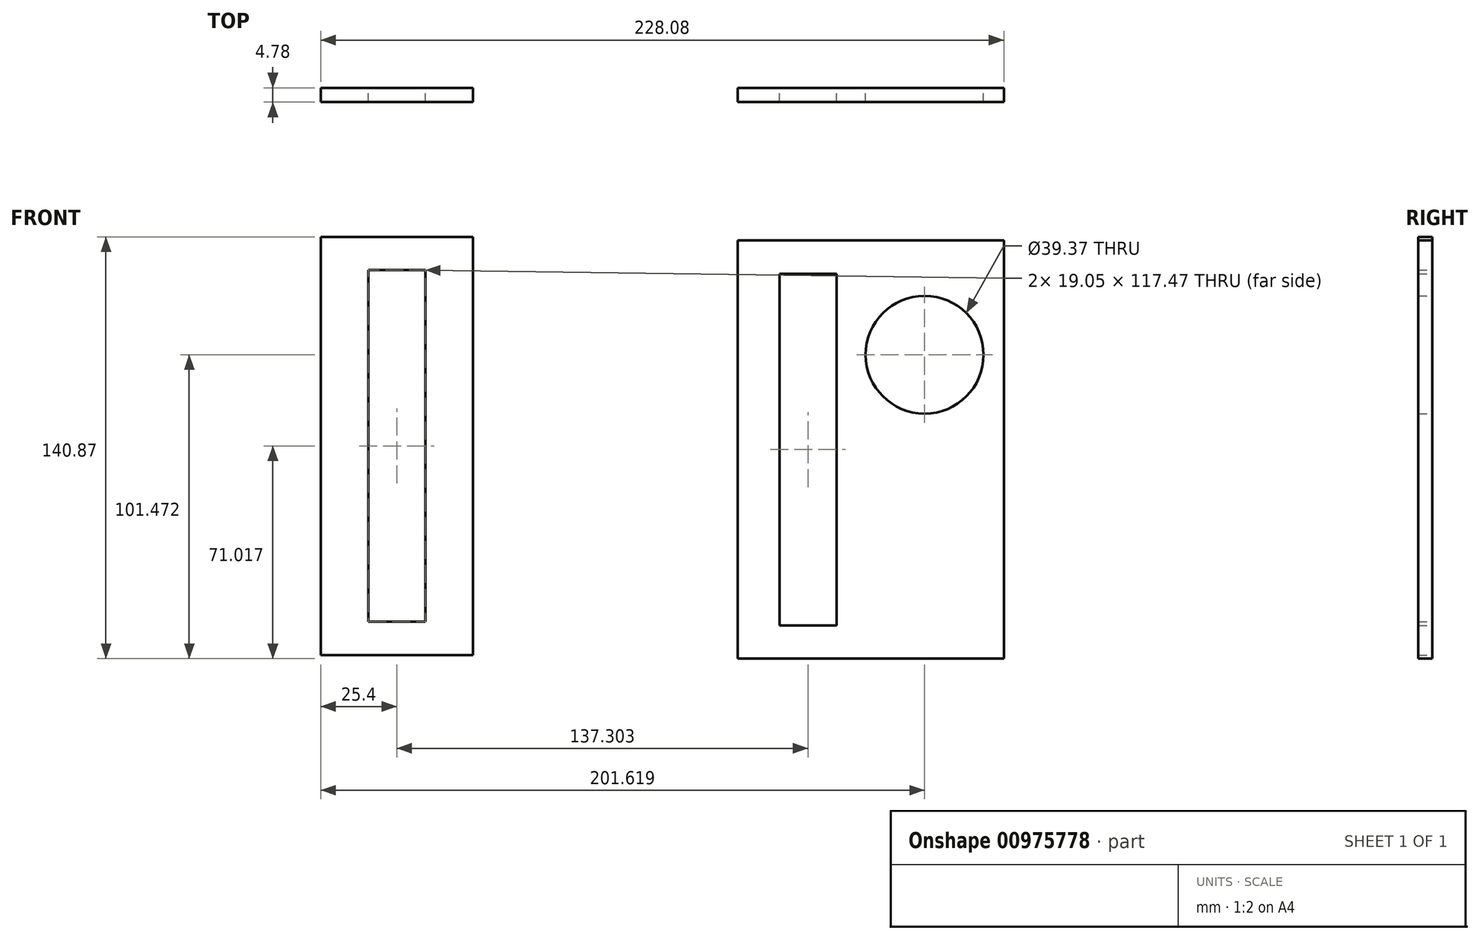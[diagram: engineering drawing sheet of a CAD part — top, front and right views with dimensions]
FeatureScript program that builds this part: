
annotation { "Feature Type Name" : "Feature", "Feature Type Description" : "" }
export const myFeature = defineFeature(function(context is Context, id is Id, definition is map)
    precondition{}
    {
        {
            var Q0;
            Q0=qCreatedBy(makeId("Front.planeOp"),FACE);
            var sketch = newSketch(context, id + "F0", { "sketchPlane" : qUnion([Q0])});
            skLineSegment(sketch, "E0.bottom", {"start": v(-130.05, 71.17) * mm, "end": v(-79.25, 71.17) * mm});
            skLineSegment(sketch, "E0.top", {"start": v(-130.05, -68.53) * mm, "end": v(-79.25, -68.53) * mm});
            skLineSegment(sketch, "E0.left", {"start": v(-130.05, 71.17) * mm, "end": v(-130.05, -68.53) * mm});
            skLineSegment(sketch, "E0.right", {"start": v(-79.25, 71.17) * mm, "end": v(-79.25, -68.53) * mm});
            skLineSegment(sketch, "E1.bottom", {"start": v(9.13, 70) * mm, "end": v(98.03, 70) * mm});
            skLineSegment(sketch, "E1.top", {"start": v(9.13, -69.7) * mm, "end": v(98.03, -69.7) * mm});
            skLineSegment(sketch, "E1.left", {"start": v(9.13, 70) * mm, "end": v(9.13, -69.7) * mm});
            skLineSegment(sketch, "E1.right", {"start": v(98.03, 70) * mm, "end": v(98.03, -69.7) * mm});
            skLineSegment(sketch, "E2.bottom", {"start": v(-114.18, 60.05) * mm, "end": v(-95.13, 60.05) * mm});
            skLineSegment(sketch, "E2.top", {"start": v(-114.18, -57.42) * mm, "end": v(-95.13, -57.42) * mm});
            skLineSegment(sketch, "E2.left", {"start": v(-114.18, 60.05) * mm, "end": v(-114.18, -57.42) * mm});
            skLineSegment(sketch, "E2.right", {"start": v(-95.13, 60.05) * mm, "end": v(-95.13, -57.42) * mm});
            skLineSegment(sketch, "E3.bottom", {"start": v(23.13, 58.85) * mm, "end": v(42.18, 58.85) * mm});
            skLineSegment(sketch, "E3.top", {"start": v(23.13, -58.63) * mm, "end": v(42.18, -58.63) * mm});
            skLineSegment(sketch, "E3.left", {"start": v(23.13, 58.85) * mm, "end": v(23.13, -58.63) * mm});
            skCircle(sketch, "E4", {"center": v(71.57, 31.77) * mm, "radius": 19.69 * mm});
            skLineSegment(sketch, "E5", {"start": v(42.18, 58.85) * mm, "end": v(42.18, -58.63) * mm});
            skSolve(sketch);
        }
        {
            var Q0;
            Q0=makeQuery(id+"F0.imprint","IMPRINT",FACE,{"disambiguationData":[TD([[makeQuery(id+"F0.imprint","IMPRINT",EDGE,{"derivedFrom":sQuery(id+"F0.wireOp",EDGE,"E0.bottom")}),-1.0]])]});
            var Q1;
            Q1=makeQuery(id+"F0.imprint","IMPRINT",FACE,{"disambiguationData":[TD([[makeQuery(id+"F0.imprint","IMPRINT",EDGE,{"derivedFrom":sQuery(id+"F0.wireOp",EDGE,"E1.bottom")}),-1.0]])]});
            extrude(context, id + "F1", {"entities" : qUnion([Q0, Q1]), "depth" : 4.78 * mm, "offsetDistance" : 25.4 * mm});
        }
    });
